# Revit family: TYCO-FPP-Zettler-SIO800 Single inputoutput module
name_source: partatom
category: Electrical Fixtures
revit_build: Autodesk Revit 2014 (Build: 20130308_1515(x64)
units: mm (PartAtom-declared; Revit-internal decimal feet)

## types (1)
- TYCO-FPP-Zettler-SIO800 Single inputoutput module
    Alarm current = 3mA
    Alarm resistor = 680Ω
    Description = The SIO800 Single Input/Output Module is designed
to provide a monitored input and a volt free relay
changeover output.
    EOL = 3k3
    Front cover = Yes
    Keynote = It consists of an input for monitoring
the status of a normally open contact and a single
changeover relay contact.
    Length = 65 mm
    Manufacturer = Tyco
    Model = Zettler- 555.800.063
    Operating Humidity = Up to 95% non condensing
    Operating Temperature = -25o to +70oC
    PCB = PCB
    Rear cover = Yes
    Standby current = 0.3mA
    Storage Temperature = -40o to +80oC
    Type Comments = SIO800 can switch up to 2A @ 24V dc
    URL = https://tycosafetyproducts-anz.com
    Voltage = 2A @ 24V dc
    Width = 85 mm
    Wire Size = Min 1.5mm2

## geometry (parser evidence)
native form markers: Sweep x7
no freeform markers — native parametric forms only
